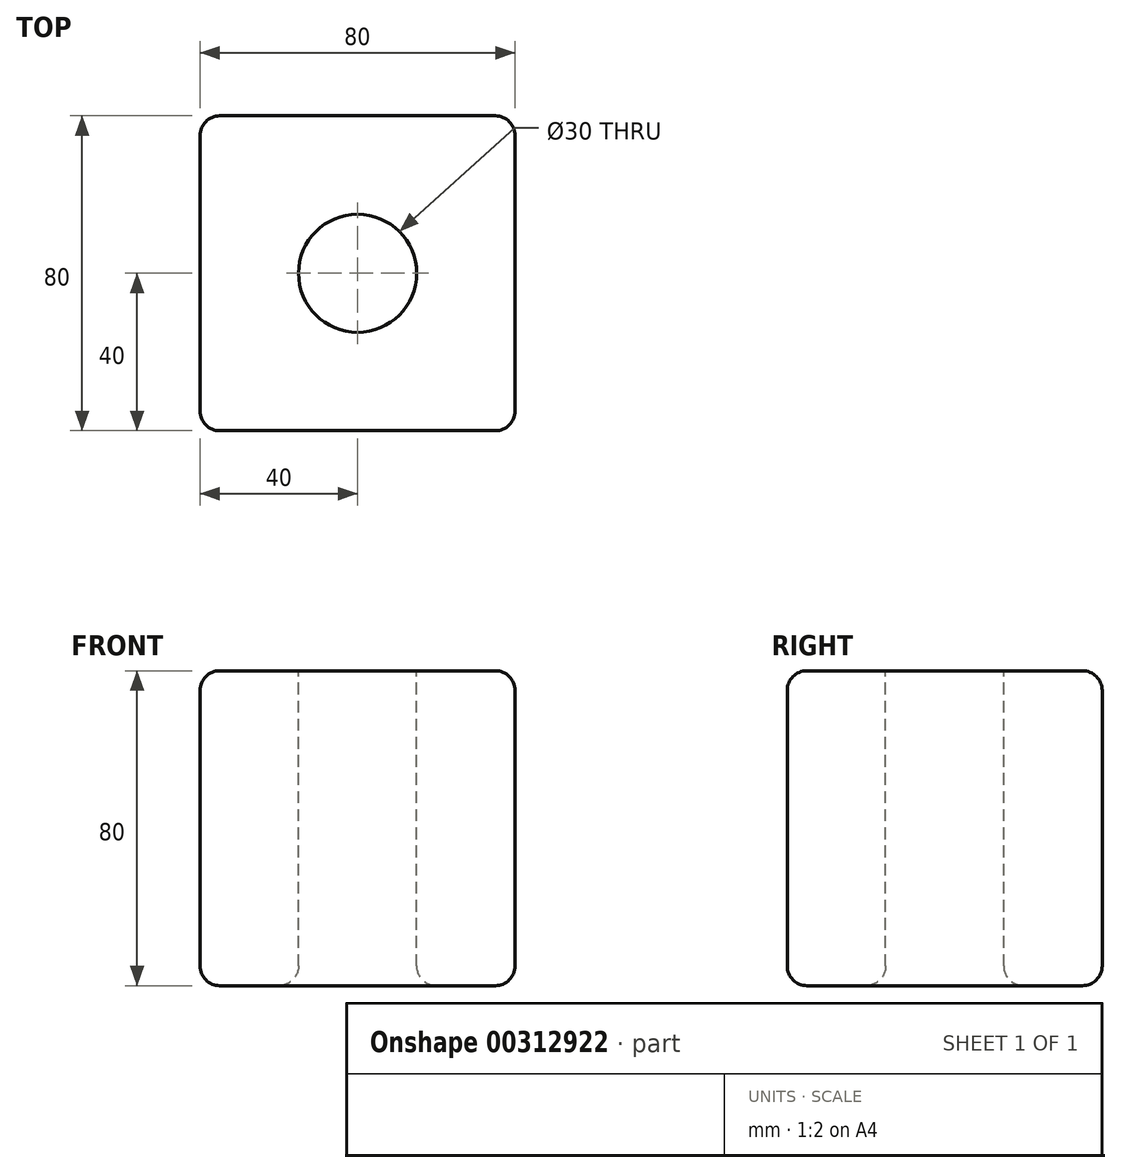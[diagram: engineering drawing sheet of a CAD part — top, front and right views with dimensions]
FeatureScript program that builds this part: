
annotation { "Feature Type Name" : "Feature", "Feature Type Description" : "" }
export const myFeature = defineFeature(function(context is Context, id is Id, definition is map)
    precondition{}
    {
        {
            var Q0;
            Q0=qCreatedBy(makeId("Top.planeOp"),FACE);
            var sketch = newSketch(context, id + "F0", { "sketchPlane" : qUnion([Q0])});
            skLineSegment(sketch, "E0.bottom", {"start": v(-40, 40) * mm, "end": v(40, 40) * mm});
            skLineSegment(sketch, "E0.top", {"start": v(-40, -40) * mm, "end": v(40, -40) * mm});
            skLineSegment(sketch, "E0.left", {"start": v(-40, 40) * mm, "end": v(-40, -40) * mm});
            skLineSegment(sketch, "E0.right", {"start": v(40, 40) * mm, "end": v(40, -40) * mm});
            skPoint(sketch, "E0.middle", {"position": v(0, 0) * mm});
            skSolve(sketch);
        }
        {
            var Q0;
            Q0=makeQuery(id+"F0.imprint","IMPRINT",FACE,{"disambiguationData":[TD([[makeQuery(id+"F0.imprint","IMPRINT",EDGE,{"derivedFrom":sQuery(id+"F0.wireOp",EDGE,"E0.bottom")}),-1.0]])]});
            extrude(context, id + "F1", {"entities" : qUnion([Q0]), "endBound" : BoundingType.SYMMETRIC, "depth" : 80 * mm});
        }
        {
            var Q0;
            Q0=makeQuery(id+"F1.opExtrude","CAP_EDGE",EDGE,{"disambiguationData":[OSD([sQuery(id+"F0.wireOp",EDGE,"E0.bottom")])],"isStart":false});
            var Q1;
            Q1=makeQuery(id+"F1.opExtrude","CAP_EDGE",EDGE,{"disambiguationData":[OSD([sQuery(id+"F0.wireOp",EDGE,"E0.left")])],"isStart":false});
            var Q2;
            Q2=makeQuery(id+"F1.opExtrude","CAP_EDGE",EDGE,{"disambiguationData":[OSD([sQuery(id+"F0.wireOp",EDGE,"E0.top")])],"isStart":false});
            var Q3;
            Q3=makeQuery(id+"F1.opExtrude","CAP_EDGE",EDGE,{"disambiguationData":[OSD([sQuery(id+"F0.wireOp",EDGE,"E0.right")])],"isStart":false});
            var Q4;
            Q4=makeQuery(id+"F1.opExtrude","CAP_EDGE",EDGE,{"disambiguationData":[OSD([sQuery(id+"F0.wireOp",EDGE,"E0.bottom")])],"isStart":true});
            var Q5;
            Q5=makeQuery(id+"F1.opExtrude","SWEPT_EDGE",EDGE,{"disambiguationData":[OSD([sQuery(id+"F0.wireOp",EDGE,"E0.bottom"),sQuery(id+"F0.wireOp",EDGE,"E0.left")])]});
            var Q6;
            Q6=makeQuery(id+"F1.opExtrude","SWEPT_EDGE",EDGE,{"disambiguationData":[OSD([sQuery(id+"F0.wireOp",EDGE,"E0.bottom"),sQuery(id+"F0.wireOp",EDGE,"E0.right")])]});
            var Q7;
            Q7=makeQuery(id+"F1.opExtrude","SWEPT_FACE",FACE,{"disambiguationData":[OSD([sQuery(id+"F0.wireOp",EDGE,"E0.left")])]});
            var Q8;
            Q8=makeQuery(id+"F1.opExtrude","CAP_EDGE",EDGE,{"disambiguationData":[OSD([sQuery(id+"F0.wireOp",EDGE,"E0.right")])],"isStart":true});
            var Q9;
            Q9=makeQuery(id+"F1.opExtrude","CAP_EDGE",EDGE,{"disambiguationData":[OSD([sQuery(id+"F0.wireOp",EDGE,"E0.top")])],"isStart":true});
            var Q10;
            Q10=makeQuery(id+"F1.opExtrude","CAP_EDGE",EDGE,{"disambiguationData":[OSD([sQuery(id+"F0.wireOp",EDGE,"E0.left")])],"isStart":true});
            var Q11;
            Q11=makeQuery(id+"F1.opExtrude","SWEPT_EDGE",EDGE,{"disambiguationData":[OSD([sQuery(id+"F0.wireOp",EDGE,"E0.top"),sQuery(id+"F0.wireOp",EDGE,"E0.right")])]});
            fillet(context, id + "F2", {"entities" : qUnion([Q0, Q1, Q2, Q3, Q4, Q5, Q6, Q7, Q8, Q9, Q10, Q11]), "radius" : 5 * mm, "tangentPropagation" : true, "allowEdgeOverflow" : false});
        }
        {
            var Q0;
            Q0=makeQuery(id+"F1.opExtrude","CAP_FACE",FACE,{"disambiguationData":[OSD([sQuery(id+"F0.wireOp",EDGE,"E0.bottom"),sQuery(id+"F0.wireOp",EDGE,"E0.top"),sQuery(id+"F0.wireOp",EDGE,"E0.left"),sQuery(id+"F0.wireOp",EDGE,"E0.right")])],"isStart":false});
            var sketch = newSketch(context, id + "F3", { "sketchPlane" : qUnion([Q0])});
            skCircle(sketch, "E1", {"center": v(0, 0) * mm, "radius": 15 * mm});
            skSolve(sketch);
        }
        {
            var Q0;
            Q0=makeQuery(id+"F3.imprint","IMPRINT",FACE,{"disambiguationData":[TD([[makeQuery(id+"F3.imprint","IMPRINT",EDGE,{"derivedFrom":sQuery(id+"F3.wireOp",EDGE,"E1")}),1.0]])]});
            extrude(context, id + "F4", {"entities" : qUnion([Q0]), "operationType" : NewBodyOperationType.REMOVE, "endBound" : BoundingType.THROUGH_ALL, "oppositeDirection" : true, "depth" : 25 * mm});
        }
        {
            var Q0;
            Q0=makeQuery(id+"F4.boolean.opBoolean","COPY",EDGE,{"derivedFrom":makeQuery(id+"F4.opExtrude","CAP_EDGE",EDGE,{"disambiguationData":[OSD([sQuery(id+"F3.wireOp",EDGE,"E1")])],"isStart":true})});
            var Q1;
            Q1=makeQuery(id+"F4.boolean.opBoolean","INTERSECT",EDGE,{"derivedFrom":[makeQuery(id+"F1.opExtrude","CAP_FACE",FACE,{"disambiguationData":[OSD([sQuery(id+"F0.wireOp",EDGE,"E0.bottom"),sQuery(id+"F0.wireOp",EDGE,"E0.top"),sQuery(id+"F0.wireOp",EDGE,"E0.left"),sQuery(id+"F0.wireOp",EDGE,"E0.right")])],"isStart":true}),makeQuery(id+"F4.opExtrude","SWEPT_FACE",FACE,{"disambiguationData":[OSD([sQuery(id+"F3.wireOp",EDGE,"E1")])]})]});
            fillet(context, id + "F5", {"entities" : qUnion([Q0, Q1]), "radius" : 5 * mm, "tangentPropagation" : true, "allowEdgeOverflow" : false});
        }
    });
